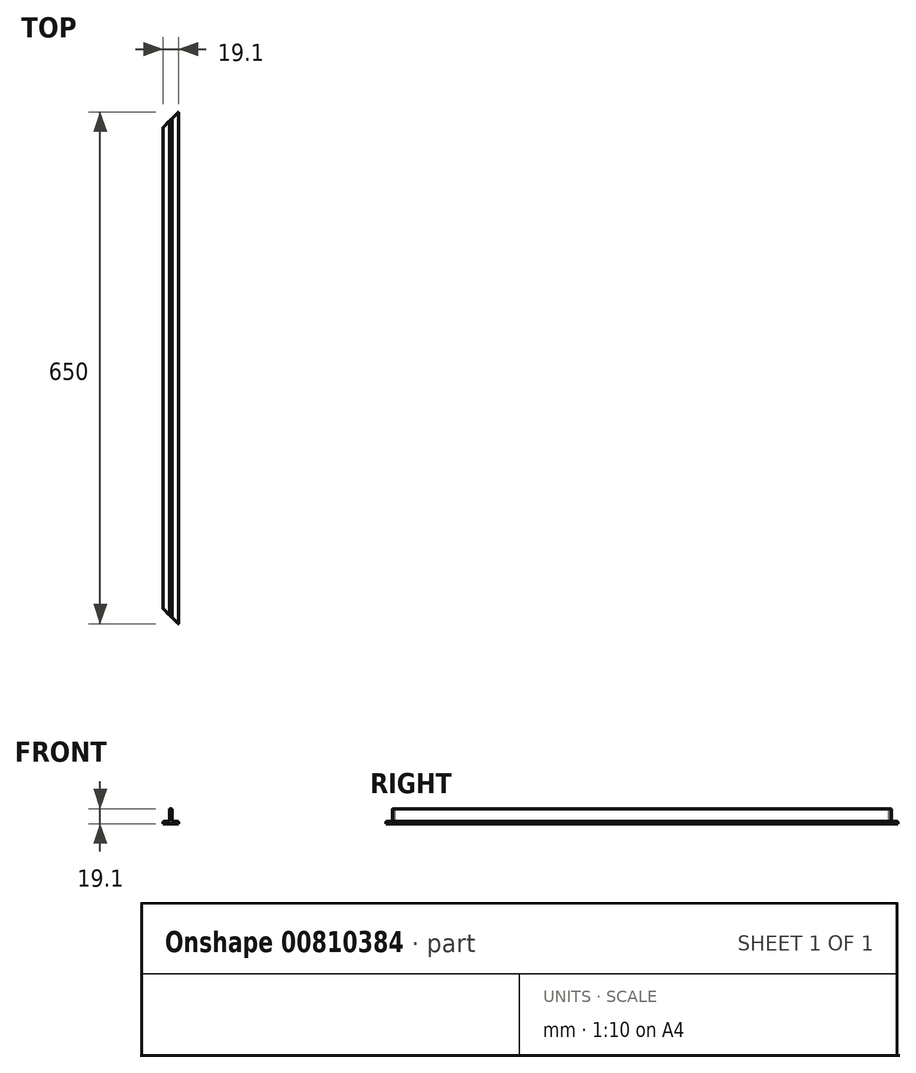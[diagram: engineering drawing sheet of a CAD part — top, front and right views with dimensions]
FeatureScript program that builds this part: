
annotation { "Feature Type Name" : "Feature", "Feature Type Description" : "" }
export const myFeature = defineFeature(function(context is Context, id is Id, definition is map)
    precondition{}
    {
        {
            var Q0;
            Q0=qCreatedBy(makeId("Front.planeOp"),FACE);
            var sketch = newSketch(context, id + "F0", { "sketchPlane" : qUnion([Q0])});
            skLineSegment(sketch, "E0", {"start": v(-9.55, 0) * mm, "end": v(9.55, 0) * mm});
            skLineSegment(sketch, "E1", {"start": v(9.55, 0) * mm, "end": v(9.55, 2.17) * mm});
            skLineSegment(sketch, "E2", {"start": v(8.55, 3.17) * mm, "end": v(2.58, 3.17) * mm});
            skLineSegment(sketch, "E3", {"start": v(1.58, 4.17) * mm, "end": v(1.58, 18.1) * mm});
            skLineSegment(sketch, "E4", {"start": v(0.58, 19.1) * mm, "end": v(-0.59, 19.1) * mm});
            skLineSegment(sketch, "E5", {"start": v(-1.59, 18.1) * mm, "end": v(-1.59, 4.17) * mm});
            skLineSegment(sketch, "E6", {"start": v(-2.59, 3.17) * mm, "end": v(-8.55, 3.17) * mm});
            skLineSegment(sketch, "E7", {"start": v(-9.55, 2.17) * mm, "end": v(-9.55, 0) * mm});
            skPoint(sketch, "E8.visualSharp", {"position": v(-9.55, 3.17) * mm});
            skArc(sketch, "E8.filletArc", {"start": v(-8.55, 3.17) * mm, "mid": v(-9.26, 2.88) * mm, "end": v(-9.55, 2.17) * mm});
            skPoint(sketch, "E9.visualSharp", {"position": v(9.55, 3.17) * mm});
            skArc(sketch, "E9.filletArc", {"start": v(9.55, 2.17) * mm, "mid": v(9.26, 2.88) * mm, "end": v(8.55, 3.17) * mm});
            skPoint(sketch, "E10.visualSharp", {"position": v(1.58, 19.1) * mm});
            skArc(sketch, "E10.filletArc", {"start": v(1.58, 18.1) * mm, "mid": v(1.3, 18.8) * mm, "end": v(0.58, 19.1) * mm});
            skPoint(sketch, "E11.visualSharp", {"position": v(-1.59, 19.1) * mm});
            skArc(sketch, "E11.filletArc", {"start": v(-0.59, 19.1) * mm, "mid": v(-1.3, 18.8) * mm, "end": v(-1.59, 18.1) * mm});
            skPoint(sketch, "E12.visualSharp", {"position": v(1.58, 3.17) * mm});
            skArc(sketch, "E12.filletArc", {"start": v(1.58, 4.17) * mm, "mid": v(1.88, 3.46) * mm, "end": v(2.58, 3.17) * mm});
            skPoint(sketch, "E13.visualSharp", {"position": v(-1.59, 3.17) * mm});
            skArc(sketch, "E13.filletArc", {"start": v(-2.59, 3.17) * mm, "mid": v(-1.88, 3.46) * mm, "end": v(-1.59, 4.17) * mm});
            skSolve(sketch);
        }
        {
            var Q0;
            Q0=makeQuery(id+"F0.imprint","IMPRINT",FACE,{"disambiguationData":[TD([[makeQuery(id+"F0.imprint","IMPRINT",EDGE,{"derivedFrom":sQuery(id+"F0.wireOp",EDGE,"E0")}),1.0]])]});
            extrude(context, id + "F1", {"entities" : qUnion([Q0]), "depth" : 650 * mm, "offsetDistance" : 25 * mm});
        }
        {
            var Q0;
            Q0=makeQuery(id+"F1.opExtrude","SWEPT_FACE",FACE,{"disambiguationData":[OSD([sQuery(id+"F0.wireOp",EDGE,"E0")])]});
            var sketch = newSketch(context, id + "F2", { "sketchPlane" : qUnion([Q0])});
            skLineSegment(sketch, "E14", {"start": v(9.55, 650) * mm, "end": v(-9.55, 650) * mm});
            skLineSegment(sketch, "E15", {"start": v(-9.55, 650) * mm, "end": v(-9.55, 630.9) * mm});
            skLineSegment(sketch, "E16", {"start": v(-9.55, 630.9) * mm, "end": v(9.55, 650) * mm});
            skLineSegment(sketch, "E17", {"start": v(9.55, 325) * mm, "end": v(-9.55, 325) * mm, "construction": true});
            skLineSegment(sketch, "E18.MirrorCS", {"start": v(9.55, 0) * mm, "end": v(-9.55, 0) * mm});
            skLineSegment(sketch, "E19.MirrorCS", {"start": v(-9.55, 19.1) * mm, "end": v(9.55, 0) * mm});
            skLineSegment(sketch, "E20.MirrorCS", {"start": v(-9.55, 0) * mm, "end": v(-9.55, 19.1) * mm});
            skSolve(sketch);
        }
        {
            var Q0;
            Q0=makeQuery(id+"F2.imprint","IMPRINT",FACE,{"disambiguationData":[TD([[makeQuery(id+"F2.imprint","IMPRINT",EDGE,{"derivedFrom":sQuery(id+"F2.wireOp",EDGE,"E14")}),-1.0]])]});
            var Q1;
            Q1=makeQuery(id+"F2.imprint","IMPRINT",FACE,{"disambiguationData":[TD([[makeQuery(id+"F2.imprint","IMPRINT",EDGE,{"derivedFrom":sQuery(id+"F2.wireOp",EDGE,"E18.MirrorCS")}),1.0]])]});
            extrude(context, id + "F3", {"entities" : qUnion([Q0, Q1]), "operationType" : NewBodyOperationType.REMOVE, "oppositeDirection" : true, "depth" : 20 * mm, "offsetDistance" : 25 * mm});
        }
    });
